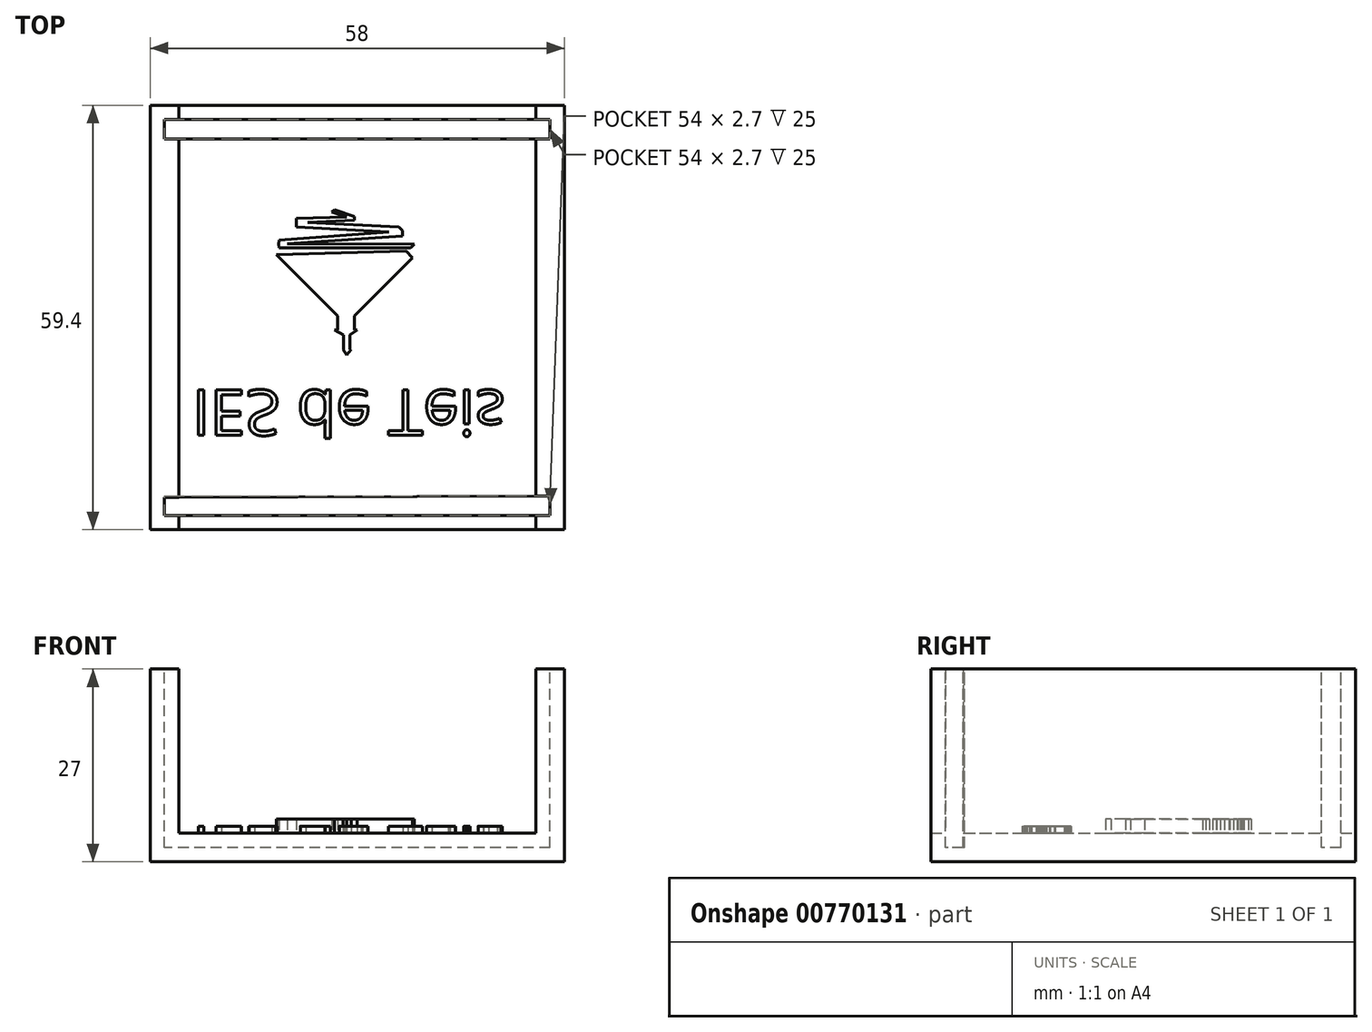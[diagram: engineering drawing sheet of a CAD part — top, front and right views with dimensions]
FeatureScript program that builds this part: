
annotation { "Feature Type Name" : "Feature", "Feature Type Description" : "" }
export const myFeature = defineFeature(function(context is Context, id is Id, definition is map)
    precondition{}
    {
        {
            var Q0;
            Q0=qCreatedBy(makeId("Front.planeOp"),FACE);
            var sketch = newSketch(context, id + "F0", { "sketchPlane" : qUnion([Q0])});
            skLineSegment(sketch, "E0.bottom", {"start": v(0, 0) * mm, "end": v(58, 0) * mm});
            skLineSegment(sketch, "E0.top", {"start": v(0, 27) * mm, "end": v(4, 27) * mm});
            skLineSegment(sketch, "E0.left", {"start": v(0, 0) * mm, "end": v(0, 27) * mm});
            skLineSegment(sketch, "E0.right", {"start": v(58, 0) * mm, "end": v(58, 27) * mm});
            skLineSegment(sketch, "E1", {"start": v(54, 27) * mm, "end": v(54, 4) * mm});
            skLineSegment(sketch, "E2", {"start": v(54, 4) * mm, "end": v(4, 4) * mm});
            skLineSegment(sketch, "E3", {"start": v(4, 4) * mm, "end": v(4, 27) * mm});
            skLineSegment(sketch, "E4.trimOffspring", {"start": v(54, 27) * mm, "end": v(58, 27) * mm});
            skSolve(sketch);
        }
        {
            var Q0;
            Q0=makeQuery(id+"F0.imprint","IMPRINT",FACE,{"disambiguationData":[TD([[makeQuery(id+"F0.imprint","IMPRINT",EDGE,{"derivedFrom":sQuery(id+"F0.wireOp",EDGE,"E0.bottom")}),1.0]])]});
            extrude(context, id + "F1", {"entities" : qUnion([Q0]), "depth" : 59.4 * mm, "offsetDistance" : 25 * mm});
        }
        {
            var Q0;
            Q0=makeQuery(id+"FwCQ9gHjEzHw4f9_1.boolean.opBoolean","MERGE",FACE,{"derivedFrom":[makeQuery(id+"F1.opExtrude","SWEPT_FACE",FACE,{"disambiguationData":[OSD([sQuery(id+"F0.wireOp",EDGE,"E0.top")])]}),makeQuery(id+"F1.opExtrude","SWEPT_FACE",FACE,{"disambiguationData":[OSD([sQuery(id+"F0.wireOp",EDGE,"E4.trimOffspring")])]}),makeQuery(id+"FwCQ9gHjEzHw4f9_1.opExtrude","SWEPT_FACE",FACE,{"disambiguationData":[OSD([sQuery(id+"FeQ3ZqFSH9PSRRd_0.wireOp",EDGE,"ztclKE2C-XFhc-xzhR-qia0-Lao7OpOa8poB")])]})]});
            var sketch = newSketch(context, id + "F2", { "sketchPlane" : qUnion([Q0])});
            skPoint(sketch, "E5", {"position": v(4, -57.4) * mm});
            skPoint(sketch, "E6", {"position": v(54, -57.4) * mm});
            skLineSegment(sketch, "E7", {"start": v(2, -54.9) * mm, "end": v(2, -57.4) * mm});
            skLineSegment(sketch, "E8", {"start": v(56, -54.7) * mm, "end": v(56, -57.4) * mm});
            skLineSegment(sketch, "E9", {"start": v(56, -54.7) * mm, "end": v(2, -54.9) * mm});
            skLineSegment(sketch, "E10", {"start": v(56, -57.4) * mm, "end": v(2, -57.4) * mm});
            skSolve(sketch);
        }
        {
            var Q0;
            {var subQ0=sQuery(id+"F2.wireOp",EDGE,"E7");Q0=makeQuery(id+"F2.imprint","IMPRINT",FACE,{"disambiguationData":[TD([[makeQuery(id+"F2.imprint","IMPRINT",EDGE,{"derivedFrom":subQ0}),1.0]])]});}
            var Q1;
            {var subQ0=sQuery(id+"F2.wireOp",EDGE,"E9");var subQ1=makeQuery(id+"F1.opExtrude","SWEPT_EDGE",EDGE,{"disambiguationData":[OSD([sQuery(id+"F0.wireOp",EDGE,"E1"),sQuery(id+"F0.wireOp",EDGE,"E4.trimOffspring")])]});var subQ2=makeQuery(id+"F2.imprint","INTERSECT",VERTEX,{"derivedFrom":[subQ1,subQ0]});Q1=makeQuery(id+"F2.imprint","IMPRINT",FACE,{"disambiguationData":[TD([[makeQuery(id+"F2.imprint","IMPRINT",EDGE,{"disambiguationData":[TD([[subQ2,-1.0]])],"derivedFrom":subQ0}),1.0]])]});}
            var Q2;
            {var subQ0=sQuery(id+"F2.wireOp",EDGE,"E8");Q2=makeQuery(id+"F2.imprint","IMPRINT",FACE,{"disambiguationData":[TD([[makeQuery(id+"F2.imprint","IMPRINT",EDGE,{"derivedFrom":subQ0}),-1.0]])]});}
            extrude(context, id + "F3", {"entities" : qUnion([Q0, Q1, Q2]), "operationType" : NewBodyOperationType.REMOVE, "oppositeDirection" : true, "depth" : 25 * mm, "offsetDistance" : 25 * mm});
        }
        {
            var Q0;
            Q0=makeQuery(id+"FwCQ9gHjEzHw4f9_1.boolean.opBoolean","MERGE",FACE,{"derivedFrom":[makeQuery(id+"F1.opExtrude","SWEPT_FACE",FACE,{"disambiguationData":[OSD([sQuery(id+"F0.wireOp",EDGE,"E0.top")])]}),makeQuery(id+"F1.opExtrude","SWEPT_FACE",FACE,{"disambiguationData":[OSD([sQuery(id+"F0.wireOp",EDGE,"E4.trimOffspring")])]}),makeQuery(id+"FwCQ9gHjEzHw4f9_1.opExtrude","SWEPT_FACE",FACE,{"disambiguationData":[OSD([sQuery(id+"FeQ3ZqFSH9PSRRd_0.wireOp",EDGE,"ztclKE2C-XFhc-xzhR-qia0-Lao7OpOa8poB")])]})]});
            var sketch = newSketch(context, id + "F4", { "sketchPlane" : qUnion([Q0])});
            skSolve(sketch);
        }
        {
            var Q0;
            Q0=makeQuery(id+"F1.opExtrude","SWEPT_FACE",FACE,{"disambiguationData":[OSD([sQuery(id+"F0.wireOp",EDGE,"E0.bottom")])]});
            var Q1;
            Q1=qBodyType(qCreatedBy(id+"F6",EDGE),BodyType.WIRE);
            cPlane(context, id + "F5", {"entities" : qUnion([Q0, Q1]), "cplaneType" : CPlaneType.OFFSET, "offset" : 2 * mm, "oppositeDirection" : true, "width" : 150 * mm, "height" : 150 * mm});
        }
        {
            var Q0;
            Q0=qCreatedBy(id+"F5.planeOp",FACE);
            var sketch = newSketch(context, id + "F6", { "sketchPlane" : qUnion([Q0])});
            skText(sketch, "E11", { "text": "IES de Teis", "fontName": "OpenSans-Regular.ttf"});
            const initialGuessF6  = {"E11": [0.0059, 0.03985, 1, 0, 0.00641]};
            skSetInitialGuess(sketch, initialGuessF6);
            skSolve(sketch);
        }
        {
            var Q0;
            Q0=qSketchRegion(id+"F6",true);
            extrude(context, id + "F7", {"entities" : qUnion([Q0]), "operationType" : NewBodyOperationType.ADD, "oppositeDirection" : true, "depth" : 3 * mm, "offsetDistance" : 25 * mm});
        }
        {
            var Q0;
            Q0=qCreatedBy(id+"F5.planeOp",FACE);
            var sketch = newSketch(context, id + "F8", { "sketchPlane" : qUnion([Q0])});
            skLineSegment(sketch, "E12", {"start": v(27.5, 34.96) * mm, "end": v(26.99, 34.16) * mm});
            skLineSegment(sketch, "E13", {"start": v(26.99, 34.16) * mm, "end": v(28.18, 34.16) * mm});
            skLineSegment(sketch, "E14", {"start": v(28.18, 34.16) * mm, "end": v(27.5, 34.96) * mm});
            skLineSegment(sketch, "E15", {"start": v(27.97, 34.16) * mm, "end": v(27.97, 32.17) * mm});
            skLineSegment(sketch, "E16", {"start": v(27.97, 32.17) * mm, "end": v(27.07, 32.17) * mm});
            skLineSegment(sketch, "E17", {"start": v(27.07, 32.17) * mm, "end": v(27.07, 34.16) * mm});
            skLineSegment(sketch, "E18", {"start": v(27.97, 32.17) * mm, "end": v(29, 31.47) * mm});
            skLineSegment(sketch, "E19", {"start": v(29, 31.47) * mm, "end": v(28.61, 31.47) * mm});
            skLineSegment(sketch, "E20", {"start": v(28.61, 31.47) * mm, "end": v(28.61, 29.48) * mm});
            skLineSegment(sketch, "E21", {"start": v(28.61, 29.48) * mm, "end": v(26.23, 29.48) * mm});
            skLineSegment(sketch, "E22", {"start": v(26.23, 29.48) * mm, "end": v(26.23, 31.45) * mm});
            skLineSegment(sketch, "E23", {"start": v(26.23, 31.45) * mm, "end": v(25.84, 31.45) * mm});
            skLineSegment(sketch, "E24", {"start": v(25.84, 31.45) * mm, "end": v(27.07, 32.17) * mm});
            skLineSegment(sketch, "E25", {"start": v(26.23, 29.48) * mm, "end": v(17.7, 20.92) * mm});
            skLineSegment(sketch, "E26", {"start": v(17.7, 20.92) * mm, "end": v(35.82, 20.41) * mm});
            skLineSegment(sketch, "E27", {"start": v(35.82, 20.41) * mm, "end": v(36.76, 21.35) * mm});
            skLineSegment(sketch, "E28", {"start": v(36.76, 21.35) * mm, "end": v(28.61, 29.48) * mm});
            skLineSegment(sketch, "E29", {"start": v(18.06, 19.99) * mm, "end": v(36.45, 19.99) * mm});
            skLineSegment(sketch, "E30", {"start": v(36.45, 19.99) * mm, "end": v(36.98, 19.46) * mm});
            skLineSegment(sketch, "E31", {"start": v(18.02, 19.45) * mm, "end": v(18.06, 19.99) * mm});
            skLineSegment(sketch, "E32", {"start": v(19.18, 19.37) * mm, "end": v(35.36, 18.3) * mm});
            skLineSegment(sketch, "E33", {"start": v(35.36, 18.3) * mm, "end": v(35.34, 17.56) * mm});
            skLineSegment(sketch, "E34", {"start": v(33.42, 17.7) * mm, "end": v(18.06, 18.9) * mm});
            skLineSegment(sketch, "E35", {"start": v(18.06, 18.9) * mm, "end": v(18.02, 19.45) * mm});
            skLineSegment(sketch, "E36", {"start": v(35.34, 17.56) * mm, "end": v(34.85, 17.07) * mm});
            skLineSegment(sketch, "E37", {"start": v(20.48, 16.51) * mm, "end": v(20.46, 17.02) * mm});
            skLineSegment(sketch, "E38", {"start": v(20.48, 16.51) * mm, "end": v(20.46, 15.81) * mm});
            skLineSegment(sketch, "E39", {"start": v(20.46, 15.81) * mm, "end": v(27.55, 15.61) * mm});
            skLineSegment(sketch, "E40", {"start": v(28.61, 15.58) * mm, "end": v(28.6, 16.11) * mm});
            skLineSegment(sketch, "E41", {"start": v(28.6, 16.11) * mm, "end": v(22.07, 16.43) * mm});
            skLineSegment(sketch, "E42", {"start": v(28.61, 15.58) * mm, "end": v(25.83, 14.6) * mm});
            skLineSegment(sketch, "E43", {"start": v(25.83, 14.6) * mm, "end": v(25.46, 14.97) * mm});
            skLineSegment(sketch, "E44", {"start": v(25.46, 14.97) * mm, "end": v(27.55, 15.61) * mm});
            skLineSegment(sketch, "E45", {"start": v(33.42, 17.7) * mm, "end": v(20.46, 17.02) * mm});
            skLineSegment(sketch, "E46", {"start": v(34.85, 17.07) * mm, "end": v(22.07, 16.43) * mm});
            skLineSegment(sketch, "E47", {"start": v(36.98, 19.46) * mm, "end": v(19.18, 19.37) * mm});
            skSolve(sketch);
        }
        {
            var Q0;
            Q0=qSketchRegion(id+"F8",true);
            var Q1;
            Q1=qSketchRegion(id+"F10",true);
            extrude(context, id + "F9", {"entities" : qUnion([Q0, Q1]), "operationType" : NewBodyOperationType.ADD, "oppositeDirection" : true, "depth" : 4 * mm, "offsetDistance" : 25 * mm});
        }
        {
            var Q0;
            {var subQ0=sQuery(id+"F0.wireOp",EDGE,"E0.top");Q0=makeQuery(id+"F4.imprint","IMPRINT",FACE,{"disambiguationData":[TD([[makeQuery(id+"F4.imprint","IMPRINT",EDGE,{"derivedFrom":makeQuery(id+"F1.opExtrude","CAP_EDGE",EDGE,{"disambiguationData":[OSD([subQ0])],"isStart":true})}),-1.0]])]});}
            var sketch = newSketch(context, id + "F10", { "sketchPlane" : qUnion([Q0])});
            skPoint(sketch, "E48", {"position": v(4, -2) * mm});
            skLineSegment(sketch, "E49.bottom", {"start": v(2, -2) * mm, "end": v(56, -2) * mm});
            skLineSegment(sketch, "E49.top", {"start": v(2, -4.7) * mm, "end": v(56, -4.7) * mm});
            skLineSegment(sketch, "E49.left", {"start": v(2, -2) * mm, "end": v(2, -4.7) * mm});
            skLineSegment(sketch, "E49.right", {"start": v(56, -2) * mm, "end": v(56, -4.7) * mm});
            skSolve(sketch);
        }
        {
            var Q0;
            Q0=qSketchRegion(id+"F10",true);
            extrude(context, id + "F11", {"entities" : qUnion([Q0]), "operationType" : NewBodyOperationType.REMOVE, "oppositeDirection" : true, "depth" : 25 * mm, "offsetDistance" : 25 * mm});
        }
    });
